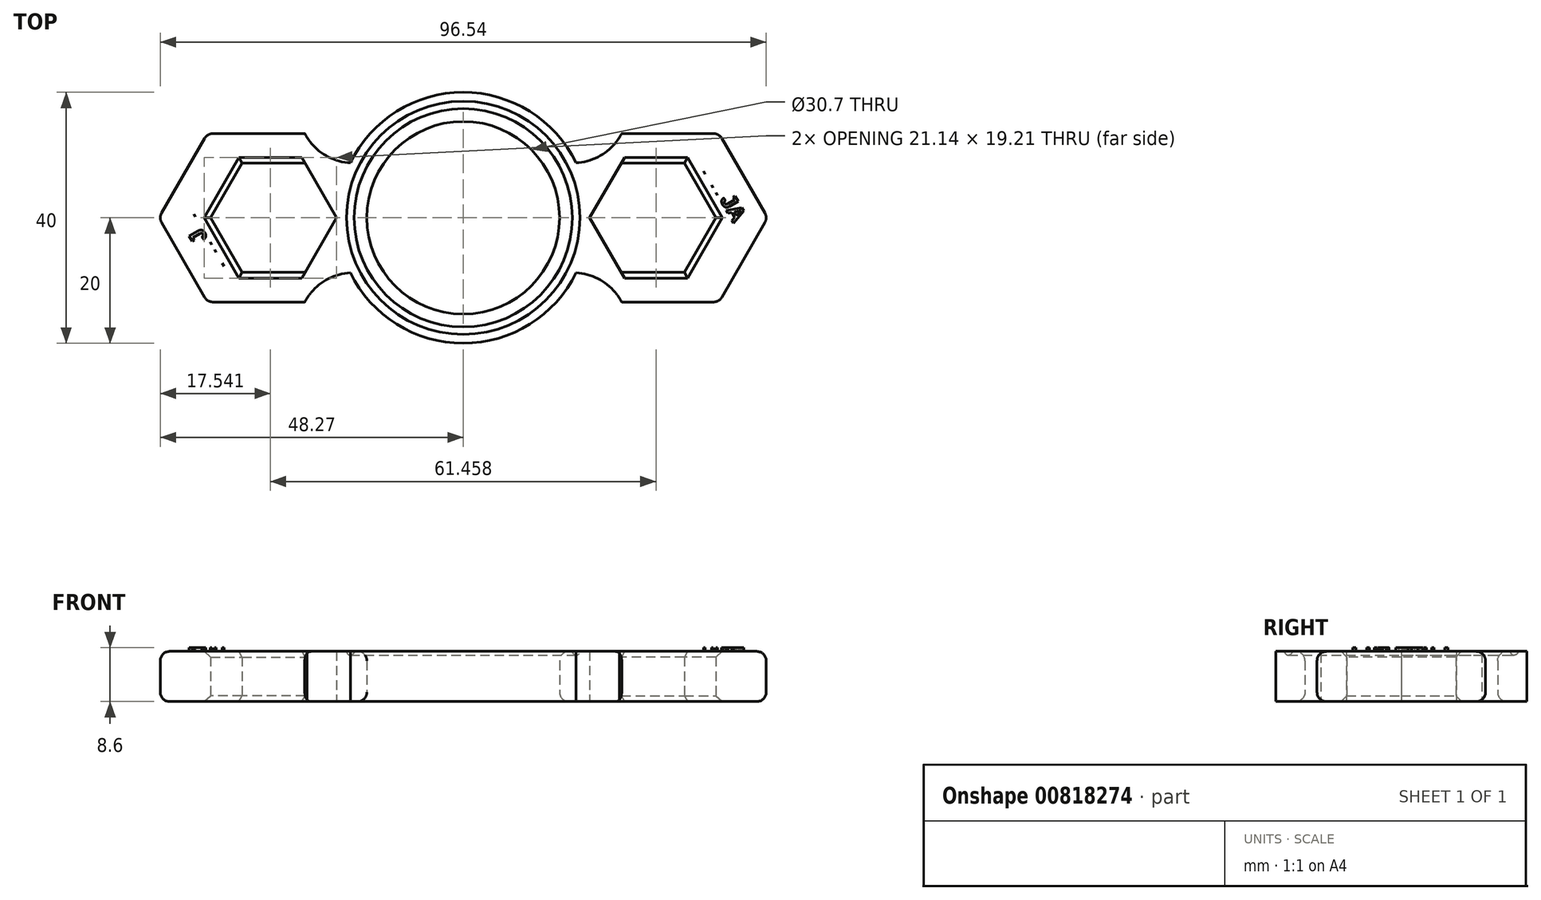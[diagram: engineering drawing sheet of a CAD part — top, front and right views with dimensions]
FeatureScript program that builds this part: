
annotation { "Feature Type Name" : "Feature", "Feature Type Description" : "" }
export const myFeature = defineFeature(function(context is Context, id is Id, definition is map)
    precondition{}
    {
        {
            var Q0;
            Q0=qCreatedBy(makeId("Top.planeOp"),FACE);
            var sketch = newSketch(context, id + "F0", { "sketchPlane" : qUnion([Q0])});
            skCircle(sketch, "E0", {"center": v(0, 0) * mm, "radius": 15.35 * mm});
            skArc(sketch, "E1", {"start": v(14.93, 9.13) * mm, "mid": v(0, 17.5) * mm, "end": v(-14.93, 9.13) * mm});
            skPoint(sketch, "E2.centerSnap0", {"position": v(-30.2, 9.1) * mm});
            skLineSegment(sketch, "E3.0", {"start": v(-24.9, -12.83) * mm, "end": v(-25.25, -13.42) * mm});
            skLineSegment(sketch, "E3.1", {"start": v(-25.25, -13.42) * mm, "end": v(-40.75, -13.42) * mm});
            skLineSegment(sketch, "E3.2", {"start": v(-40.75, -13.42) * mm, "end": v(-48.5, 0) * mm});
            skLineSegment(sketch, "E3.3", {"start": v(-48.5, 0) * mm, "end": v(-40.75, 13.42) * mm});
            skLineSegment(sketch, "E3.4", {"start": v(-40.75, 13.42) * mm, "end": v(-25.25, 13.42) * mm});
            skLineSegment(sketch, "E3.5", {"start": v(-25.25, 13.42) * mm, "end": v(-24.9, 12.83) * mm});
            skLineSegment(sketch, "E4.0", {"start": v(24.9, 12.83) * mm, "end": v(25.25, 13.42) * mm});
            skLineSegment(sketch, "E4.1", {"start": v(25.25, 13.42) * mm, "end": v(40.75, 13.42) * mm});
            skLineSegment(sketch, "E4.2", {"start": v(40.75, 13.42) * mm, "end": v(48.5, 0) * mm});
            skLineSegment(sketch, "E4.3", {"start": v(48.5, 0) * mm, "end": v(40.75, -13.42) * mm});
            skLineSegment(sketch, "E4.4", {"start": v(40.75, -13.42) * mm, "end": v(25.25, -13.42) * mm});
            skLineSegment(sketch, "E4.5", {"start": v(25.25, -13.42) * mm, "end": v(24.9, -12.83) * mm});
            skArc(sketch, "E5", {"start": v(14.93, 9.13) * mm, "mid": v(20.86, 9.42) * mm, "end": v(25.25, 13.42) * mm});
            skArc(sketch, "E6.trimOffspring", {"start": v(25.25, -13.42) * mm, "mid": v(20.86, -9.42) * mm, "end": v(14.93, -9.13) * mm});
            skPoint(sketch, "E7.center.orphan", {"position": v(33, 0) * mm});
            skPoint(sketch, "E8.center.orphan", {"position": v(0, -17.5) * mm});
            skPoint(sketch, "E9.start.orphan", {"position": v(17.5, 0) * mm});
            skArc(sketch, "E10", {"start": v(-14.93, -9.13) * mm, "mid": v(-20.86, -9.42) * mm, "end": v(-25.25, -13.42) * mm});
            skArc(sketch, "E11.trimOffspring", {"start": v(-14.93, -9.13) * mm, "mid": v(0, -17.5) * mm, "end": v(14.93, -9.13) * mm});
            skArc(sketch, "E12", {"start": v(-25.25, 13.42) * mm, "mid": v(-20.86, 9.42) * mm, "end": v(-14.93, 9.13) * mm});
            skPoint(sketch, "E2.center.orphan", {"position": v(-30.2, 0) * mm});
            skPoint(sketch, "E13.center.orphan", {"position": v(0, 17.5) * mm});
            skCircle(sketch, "E14.cCircle", {"center": v(-30.2, 0) * mm, "radius": 10.05 * mm, "construction": true});
            skLineSegment(sketch, "E14.0", {"start": v(-20.16, 0) * mm, "end": v(-25.18, -8.7) * mm});
            skLineSegment(sketch, "E14.1", {"start": v(-25.18, -8.7) * mm, "end": v(-35.23, -8.7) * mm});
            skLineSegment(sketch, "E14.2", {"start": v(-35.23, -8.7) * mm, "end": v(-40.26, 0) * mm});
            skLineSegment(sketch, "E14.3", {"start": v(-40.26, 0) * mm, "end": v(-35.23, 8.7) * mm});
            skLineSegment(sketch, "E14.4", {"start": v(-35.23, 8.7) * mm, "end": v(-25.18, 8.7) * mm});
            skLineSegment(sketch, "E14.5", {"start": v(-25.18, 8.7) * mm, "end": v(-20.16, 0) * mm});
            skPoint(sketch, "E15", {"position": v(-27, 0) * mm});
            skCircle(sketch, "E16.cCircle", {"center": v(30.2, 0) * mm, "radius": 10.05 * mm, "construction": true});
            skLineSegment(sketch, "E16.0", {"start": v(20.16, 0) * mm, "end": v(25.18, 8.7) * mm});
            skLineSegment(sketch, "E16.1", {"start": v(25.18, 8.7) * mm, "end": v(35.23, 8.7) * mm});
            skLineSegment(sketch, "E16.2", {"start": v(35.23, 8.7) * mm, "end": v(40.26, 0) * mm});
            skLineSegment(sketch, "E16.3", {"start": v(40.26, 0) * mm, "end": v(35.23, -8.7) * mm});
            skLineSegment(sketch, "E16.4", {"start": v(35.23, -8.7) * mm, "end": v(25.18, -8.7) * mm});
            skLineSegment(sketch, "E16.5", {"start": v(25.18, -8.7) * mm, "end": v(20.16, 0) * mm});
            skCircle(sketch, "E17", {"center": v(0, 0) * mm, "radius": 20 * mm});
            skLineSegment(sketch, "E18", {"start": v(-24.9, 12.83) * mm, "end": v(-15.35, 12.83) * mm});
            skSolve(sketch);
        }
        {
            var Q0;
            {var subQ0=sQuery(id+"F0.wireOp",EDGE,"E3.0");Q0=makeQuery(id+"F0.imprint","IMPRINT",FACE,{"disambiguationData":[TD([[makeQuery(id+"F0.imprint","IMPRINT",EDGE,{"derivedFrom":subQ0}),-1.0]])]});}
            var Q1;
            {var subQ0=sQuery(id+"F0.wireOp",EDGE,"E3.5");Q1=makeQuery(id+"F0.imprint","IMPRINT",FACE,{"disambiguationData":[TD([[makeQuery(id+"F0.imprint","IMPRINT",EDGE,{"derivedFrom":subQ0}),-1.0]])]});}
            var Q2;
            {var subQ0=sQuery(id+"F0.wireOp",EDGE,"E4.0");Q2=makeQuery(id+"F0.imprint","IMPRINT",FACE,{"disambiguationData":[TD([[makeQuery(id+"F0.imprint","IMPRINT",EDGE,{"derivedFrom":subQ0}),-1.0]])]});}
            var Q3;
            {var subQ0=sQuery(id+"F0.wireOp",EDGE,"E4.5");Q3=makeQuery(id+"F0.imprint","IMPRINT",FACE,{"disambiguationData":[TD([[makeQuery(id+"F0.imprint","IMPRINT",EDGE,{"derivedFrom":subQ0}),-1.0]])]});}
            var Q4;
            {var subQ0=sQuery(id+"F0.wireOp",EDGE,"E11.trimOffspring");Q4=makeQuery(id+"F0.imprint","IMPRINT",FACE,{"disambiguationData":[TD([[makeQuery(id+"F0.imprint","IMPRINT",EDGE,{"derivedFrom":subQ0}),-1.0]])]});}
            var Q5;
            {var subQ4=sQuery(id+"F0.wireOp",EDGE,"E1");Q5=makeQuery(id+"F0.imprint","IMPRINT",FACE,{"disambiguationData":[TD([[makeQuery(id+"F0.imprint","IMPRINT",EDGE,{"derivedFrom":subQ4}),-1.0]])]});}
            var Q6;
            {var subQ9=sQuery(id+"F0.wireOp",EDGE,"E4.1");Q6=makeQuery(id+"F0.imprint","IMPRINT",FACE,{"disambiguationData":[TD([[makeQuery(id+"F0.imprint","IMPRINT",EDGE,{"derivedFrom":subQ9}),-1.0]])]});}
            var Q7;
            Q7=makeQuery(id+"F0.imprint","IMPRINT",FACE,{"disambiguationData":[TD([[makeQuery(id+"F0.imprint","IMPRINT",EDGE,{"derivedFrom":sQuery(id+"F0.wireOp",EDGE,"E0")}),-1.0]])]});
            var Q8;
            {var subQ7=sQuery(id+"F0.wireOp",EDGE,"E3.1");Q8=makeQuery(id+"F0.imprint","IMPRINT",FACE,{"disambiguationData":[TD([[makeQuery(id+"F0.imprint","IMPRINT",EDGE,{"derivedFrom":subQ7}),-1.0]])]});}
            extrude(context, id + "F1", {"entities" : qUnion([Q0, Q1, Q2, Q3, Q4, Q5, Q6, Q7, Q8]), "endBound" : BoundingType.SYMMETRIC, "depth" : 8 * mm, "offsetDistance" : 25 * mm});
        }
        {
            var Q0;
            Q0=makeQuery(id+"F1.opExtrude","CAP_EDGE",EDGE,{"disambiguationData":[OSD([sQuery(id+"F0.wireOp",EDGE,"E4.2")])],"isStart":true});
            var Q1;
            Q1=makeQuery(id+"F1.opExtrude","SWEPT_EDGE",EDGE,{"disambiguationData":[OSD([sQuery(id+"F0.wireOp",EDGE,"E4.1"),sQuery(id+"F0.wireOp",EDGE,"E4.2")])]});
            var Q2;
            Q2=makeQuery(id+"F1.opExtrude","CAP_EDGE",EDGE,{"disambiguationData":[OSD([sQuery(id+"F0.wireOp",EDGE,"E4.2")])],"isStart":false});
            var Q3;
            Q3=makeQuery(id+"F1.opExtrude","SWEPT_EDGE",EDGE,{"disambiguationData":[OSD([sQuery(id+"F0.wireOp",EDGE,"E4.2"),sQuery(id+"F0.wireOp",EDGE,"E4.3")])]});
            var Q4;
            Q4=makeQuery(id+"F1.opExtrude","CAP_EDGE",EDGE,{"disambiguationData":[OSD([sQuery(id+"F0.wireOp",EDGE,"E4.1")])],"isStart":true});
            var Q5;
            Q5=makeQuery(id+"F1.opExtrude","CAP_EDGE",EDGE,{"disambiguationData":[OSD([sQuery(id+"F0.wireOp",EDGE,"E4.1")])],"isStart":false});
            var Q6;
            Q6=makeQuery(id+"F1.opExtrude","CAP_EDGE",EDGE,{"disambiguationData":[OSD([sQuery(id+"F0.wireOp",EDGE,"E4.4")])],"isStart":false});
            var Q7;
            Q7=makeQuery(id+"F1.opExtrude","CAP_EDGE",EDGE,{"disambiguationData":[OSD([sQuery(id+"F0.wireOp",EDGE,"E4.3")])],"isStart":false});
            var Q8;
            Q8=makeQuery(id+"F1.opExtrude","SWEPT_EDGE",EDGE,{"disambiguationData":[OSD([sQuery(id+"F0.wireOp",EDGE,"E4.3"),sQuery(id+"F0.wireOp",EDGE,"E4.4")])]});
            var Q9;
            Q9=makeQuery(id+"F1.opExtrude","CAP_EDGE",EDGE,{"disambiguationData":[OSD([sQuery(id+"F0.wireOp",EDGE,"E4.3")])],"isStart":true});
            var Q10;
            Q10=makeQuery(id+"F1.opExtrude","CAP_EDGE",EDGE,{"disambiguationData":[OSD([sQuery(id+"F0.wireOp",EDGE,"E4.4")])],"isStart":true});
            var Q11;
            Q11=makeQuery(id+"F1.opExtrude","CAP_EDGE",EDGE,{"disambiguationData":[OSD([sQuery(id+"F0.wireOp",EDGE,"E3.1")])],"isStart":true});
            var Q12;
            Q12=makeQuery(id+"F1.opExtrude","CAP_EDGE",EDGE,{"disambiguationData":[OSD([sQuery(id+"F0.wireOp",EDGE,"E3.2")])],"isStart":true});
            var Q13;
            Q13=makeQuery(id+"F1.opExtrude","CAP_EDGE",EDGE,{"disambiguationData":[OSD([sQuery(id+"F0.wireOp",EDGE,"E3.3")])],"isStart":true});
            var Q14;
            Q14=makeQuery(id+"F1.opExtrude","CAP_EDGE",EDGE,{"disambiguationData":[OSD([sQuery(id+"F0.wireOp",EDGE,"E3.4")])],"isStart":true});
            var Q15;
            Q15=makeQuery(id+"F1.opExtrude","CAP_EDGE",EDGE,{"disambiguationData":[OSD([sQuery(id+"F0.wireOp",EDGE,"E3.3")])],"isStart":false});
            var Q16;
            Q16=makeQuery(id+"F1.opExtrude","SWEPT_EDGE",EDGE,{"disambiguationData":[OSD([sQuery(id+"F0.wireOp",EDGE,"E3.2"),sQuery(id+"F0.wireOp",EDGE,"E3.3")])]});
            var Q17;
            Q17=makeQuery(id+"F1.opExtrude","CAP_EDGE",EDGE,{"disambiguationData":[OSD([sQuery(id+"F0.wireOp",EDGE,"E3.2")])],"isStart":false});
            var Q18;
            Q18=makeQuery(id+"F1.opExtrude","CAP_EDGE",EDGE,{"disambiguationData":[OSD([sQuery(id+"F0.wireOp",EDGE,"E3.1")])],"isStart":false});
            var Q19;
            Q19=makeQuery(id+"F1.opExtrude","SWEPT_EDGE",EDGE,{"disambiguationData":[OSD([sQuery(id+"F0.wireOp",EDGE,"E3.1"),sQuery(id+"F0.wireOp",EDGE,"E3.2")])]});
            var Q20;
            Q20=makeQuery(id+"F1.opExtrude","SWEPT_EDGE",EDGE,{"disambiguationData":[OSD([sQuery(id+"F0.wireOp",EDGE,"E3.3"),sQuery(id+"F0.wireOp",EDGE,"E3.4")])]});
            var Q21;
            Q21=makeQuery(id+"F1.opExtrude","CAP_EDGE",EDGE,{"disambiguationData":[OSD([sQuery(id+"F0.wireOp",EDGE,"E3.4")])],"isStart":false});
            var Q22;
            Q22=makeQuery(id+"F1.opExtrude","CAP_EDGE",EDGE,{"disambiguationData":[OSD([sQuery(id+"F0.wireOp",EDGE,"6d71efc6-a7b5-46e8-b336-96c0588495bb.4")])],"isStart":false});
            var Q23;
            Q23=makeQuery(id+"F1.opExtrude","CAP_EDGE",EDGE,{"disambiguationData":[OSD([sQuery(id+"F0.wireOp",EDGE,"6d71efc6-a7b5-46e8-b336-96c0588495bb.5")])],"isStart":false});
            var Q24;
            Q24=makeQuery(id+"F1.opExtrude","CAP_EDGE",EDGE,{"disambiguationData":[OSD([sQuery(id+"F0.wireOp",EDGE,"6d71efc6-a7b5-46e8-b336-96c0588495bb.0")])],"isStart":false});
            var Q25;
            Q25=makeQuery(id+"F1.opExtrude","CAP_EDGE",EDGE,{"disambiguationData":[OSD([sQuery(id+"F0.wireOp",EDGE,"6d71efc6-a7b5-46e8-b336-96c0588495bb.1")])],"isStart":false});
            var Q26;
            Q26=makeQuery(id+"F1.opExtrude","CAP_EDGE",EDGE,{"disambiguationData":[OSD([sQuery(id+"F0.wireOp",EDGE,"6d71efc6-a7b5-46e8-b336-96c0588495bb.2")])],"isStart":false});
            var Q27;
            Q27=makeQuery(id+"F1.opExtrude","CAP_EDGE",EDGE,{"disambiguationData":[OSD([sQuery(id+"F0.wireOp",EDGE,"6d71efc6-a7b5-46e8-b336-96c0588495bb.3")])],"isStart":false});
            var Q28;
            Q28=makeQuery(id+"F1.opExtrude","CAP_EDGE",EDGE,{"disambiguationData":[OSD([sQuery(id+"F0.wireOp",EDGE,"6d71efc6-a7b5-46e8-b336-96c0588495bb.0")])],"isStart":true});
            var Q29;
            Q29=makeQuery(id+"F1.opExtrude","CAP_EDGE",EDGE,{"disambiguationData":[OSD([sQuery(id+"F0.wireOp",EDGE,"6d71efc6-a7b5-46e8-b336-96c0588495bb.5")])],"isStart":true});
            var Q30;
            Q30=makeQuery(id+"F1.opExtrude","CAP_EDGE",EDGE,{"disambiguationData":[OSD([sQuery(id+"F0.wireOp",EDGE,"6d71efc6-a7b5-46e8-b336-96c0588495bb.4")])],"isStart":true});
            var Q31;
            Q31=makeQuery(id+"F1.opExtrude","CAP_EDGE",EDGE,{"disambiguationData":[OSD([sQuery(id+"F0.wireOp",EDGE,"6d71efc6-a7b5-46e8-b336-96c0588495bb.3")])],"isStart":true});
            var Q32;
            Q32=makeQuery(id+"F1.opExtrude","CAP_EDGE",EDGE,{"disambiguationData":[OSD([sQuery(id+"F0.wireOp",EDGE,"6d71efc6-a7b5-46e8-b336-96c0588495bb.2")])],"isStart":true});
            var Q33;
            Q33=makeQuery(id+"F1.opExtrude","CAP_EDGE",EDGE,{"disambiguationData":[OSD([sQuery(id+"F0.wireOp",EDGE,"6d71efc6-a7b5-46e8-b336-96c0588495bb.1")])],"isStart":true});
            var Q34;
            Q34=makeQuery(id+"F1.opExtrude","CAP_EDGE",EDGE,{"disambiguationData":[OSD([sQuery(id+"F0.wireOp",EDGE,"79f7cf52-5bca-44dd-9481-65be4d3bd6c9.5")])],"isStart":true});
            var Q35;
            Q35=makeQuery(id+"F1.opExtrude","CAP_EDGE",EDGE,{"disambiguationData":[OSD([sQuery(id+"F0.wireOp",EDGE,"79f7cf52-5bca-44dd-9481-65be4d3bd6c9.4")])],"isStart":true});
            var Q36;
            Q36=makeQuery(id+"F1.opExtrude","CAP_EDGE",EDGE,{"disambiguationData":[OSD([sQuery(id+"F0.wireOp",EDGE,"79f7cf52-5bca-44dd-9481-65be4d3bd6c9.3")])],"isStart":true});
            var Q37;
            Q37=makeQuery(id+"F1.opExtrude","CAP_EDGE",EDGE,{"disambiguationData":[OSD([sQuery(id+"F0.wireOp",EDGE,"79f7cf52-5bca-44dd-9481-65be4d3bd6c9.2")])],"isStart":true});
            var Q38;
            Q38=makeQuery(id+"F1.opExtrude","CAP_EDGE",EDGE,{"disambiguationData":[OSD([sQuery(id+"F0.wireOp",EDGE,"79f7cf52-5bca-44dd-9481-65be4d3bd6c9.1")])],"isStart":true});
            var Q39;
            Q39=makeQuery(id+"F1.opExtrude","CAP_EDGE",EDGE,{"disambiguationData":[OSD([sQuery(id+"F0.wireOp",EDGE,"79f7cf52-5bca-44dd-9481-65be4d3bd6c9.0")])],"isStart":true});
            var Q40;
            Q40=makeQuery(id+"F1.opExtrude","CAP_EDGE",EDGE,{"disambiguationData":[OSD([sQuery(id+"F0.wireOp",EDGE,"79f7cf52-5bca-44dd-9481-65be4d3bd6c9.4")])],"isStart":false});
            var Q41;
            Q41=makeQuery(id+"F1.opExtrude","CAP_EDGE",EDGE,{"disambiguationData":[OSD([sQuery(id+"F0.wireOp",EDGE,"79f7cf52-5bca-44dd-9481-65be4d3bd6c9.3")])],"isStart":false});
            var Q42;
            Q42=makeQuery(id+"F1.opExtrude","CAP_EDGE",EDGE,{"disambiguationData":[OSD([sQuery(id+"F0.wireOp",EDGE,"79f7cf52-5bca-44dd-9481-65be4d3bd6c9.2")])],"isStart":false});
            var Q43;
            Q43=makeQuery(id+"F1.opExtrude","CAP_EDGE",EDGE,{"disambiguationData":[OSD([sQuery(id+"F0.wireOp",EDGE,"79f7cf52-5bca-44dd-9481-65be4d3bd6c9.5")])],"isStart":false});
            var Q44;
            Q44=makeQuery(id+"F1.opExtrude","CAP_EDGE",EDGE,{"disambiguationData":[OSD([sQuery(id+"F0.wireOp",EDGE,"79f7cf52-5bca-44dd-9481-65be4d3bd6c9.0")])],"isStart":false});
            var Q45;
            Q45=makeQuery(id+"F1.opExtrude","CAP_EDGE",EDGE,{"disambiguationData":[OSD([sQuery(id+"F0.wireOp",EDGE,"79f7cf52-5bca-44dd-9481-65be4d3bd6c9.1")])],"isStart":false});
            var Q46;
            Q46=makeQuery(id+"F1.opExtrude","CAP_EDGE",EDGE,{"disambiguationData":[OSD([sQuery(id+"F0.wireOp",EDGE,"E0")])],"isStart":false});
            var Q47;
            Q47=makeQuery(id+"F1.opExtrude","CAP_EDGE",EDGE,{"disambiguationData":[OSD([sQuery(id+"F0.wireOp",EDGE,"E0")])],"isStart":true});
            fillet(context, id + "F2", {"entities" : qUnion([Q0, Q1, Q2, Q3, Q4, Q5, Q6, Q7, Q8, Q9, Q10, Q11, Q12, Q13, Q14, Q15, Q16, Q17, Q18, Q19, Q20, Q21, Q22, Q23, Q24, Q25, Q26, Q27, Q28, Q29, Q30, Q31, Q32, Q33, Q34, Q35, Q36, Q37, Q38, Q39, Q40, Q41, Q42, Q43, Q44, Q45, Q46, Q47]), "radius" : 1.5 * mm, "tangentPropagation" : true, "allowEdgeOverflow" : false});
        }
        {
            var Q0;
            Q0=makeQuery(id+"F1.opExtrude","CAP_EDGE",EDGE,{"disambiguationData":[OSD([sQuery(id+"F0.wireOp",EDGE,"E16.1")])],"isStart":false});
            var Q1;
            Q1=makeQuery(id+"F1.opExtrude","CAP_EDGE",EDGE,{"disambiguationData":[OSD([sQuery(id+"F0.wireOp",EDGE,"E16.1")])],"isStart":true});
            var Q2;
            Q2=makeQuery(id+"F1.opExtrude","CAP_EDGE",EDGE,{"disambiguationData":[OSD([sQuery(id+"F0.wireOp",EDGE,"E16.2")])],"isStart":true});
            var Q3;
            Q3=makeQuery(id+"F1.opExtrude","CAP_EDGE",EDGE,{"disambiguationData":[OSD([sQuery(id+"F0.wireOp",EDGE,"E16.2")])],"isStart":false});
            var Q4;
            Q4=makeQuery(id+"F1.opExtrude","CAP_EDGE",EDGE,{"disambiguationData":[OSD([sQuery(id+"F0.wireOp",EDGE,"E16.3")])],"isStart":false});
            var Q5;
            Q5=makeQuery(id+"F1.opExtrude","CAP_EDGE",EDGE,{"disambiguationData":[OSD([sQuery(id+"F0.wireOp",EDGE,"E16.3")])],"isStart":true});
            var Q6;
            Q6=makeQuery(id+"F1.opExtrude","CAP_EDGE",EDGE,{"disambiguationData":[OSD([sQuery(id+"F0.wireOp",EDGE,"E16.4")])],"isStart":false});
            var Q7;
            Q7=makeQuery(id+"F1.opExtrude","CAP_EDGE",EDGE,{"disambiguationData":[OSD([sQuery(id+"F0.wireOp",EDGE,"E14.4")])],"isStart":false});
            var Q8;
            Q8=makeQuery(id+"F1.opExtrude","CAP_EDGE",EDGE,{"disambiguationData":[OSD([sQuery(id+"F0.wireOp",EDGE,"E14.3")])],"isStart":false});
            var Q9;
            Q9=makeQuery(id+"F1.opExtrude","CAP_EDGE",EDGE,{"disambiguationData":[OSD([sQuery(id+"F0.wireOp",EDGE,"E14.2")])],"isStart":false});
            var Q10;
            Q10=makeQuery(id+"F1.opExtrude","CAP_EDGE",EDGE,{"disambiguationData":[OSD([sQuery(id+"F0.wireOp",EDGE,"E14.1")])],"isStart":false});
            var Q11;
            Q11=makeQuery(id+"F1.opExtrude","CAP_EDGE",EDGE,{"disambiguationData":[OSD([sQuery(id+"F0.wireOp",EDGE,"E16.4")])],"isStart":true});
            var Q12;
            Q12=makeQuery(id+"F1.opExtrude","CAP_EDGE",EDGE,{"disambiguationData":[OSD([sQuery(id+"F0.wireOp",EDGE,"E14.3")])],"isStart":true});
            var Q13;
            Q13=makeQuery(id+"F1.opExtrude","CAP_EDGE",EDGE,{"disambiguationData":[OSD([sQuery(id+"F0.wireOp",EDGE,"E14.2")])],"isStart":true});
            var Q14;
            Q14=makeQuery(id+"F1.opExtrude","CAP_EDGE",EDGE,{"disambiguationData":[OSD([sQuery(id+"F0.wireOp",EDGE,"E14.1")])],"isStart":true});
            var Q15;
            Q15=makeQuery(id+"F1.opExtrude","CAP_EDGE",EDGE,{"disambiguationData":[OSD([sQuery(id+"F0.wireOp",EDGE,"E14.4")])],"isStart":true});
            chamfer(context, id + "F3", {"entities" : qUnion([Q0, Q1, Q2, Q3, Q4, Q5, Q6, Q7, Q8, Q9, Q10, Q11, Q12, Q13, Q14, Q15]), "width" : 0.9 * mm, "tangentPropagation" : true});
        }
        {
            var Q0;
            Q0=makeQuery(id+"F1.opExtrude","CAP_FACE",FACE,{"disambiguationData":[OSD([sQuery(id+"F0.wireOp",EDGE,"E0"),sQuery(id+"F0.wireOp",EDGE,"E3.0"),sQuery(id+"F0.wireOp",EDGE,"E3.1"),sQuery(id+"F0.wireOp",EDGE,"E3.2"),sQuery(id+"F0.wireOp",EDGE,"E3.3"),sQuery(id+"F0.wireOp",EDGE,"E3.4"),sQuery(id+"F0.wireOp",EDGE,"E3.5"),sQuery(id+"F0.wireOp",EDGE,"E4.0"),sQuery(id+"F0.wireOp",EDGE,"E4.1"),sQuery(id+"F0.wireOp",EDGE,"E4.2"),sQuery(id+"F0.wireOp",EDGE,"E4.3"),sQuery(id+"F0.wireOp",EDGE,"E4.4"),sQuery(id+"F0.wireOp",EDGE,"E4.5"),sQuery(id+"F0.wireOp",EDGE,"E5"),sQuery(id+"F0.wireOp",EDGE,"E6.trimOffspring"),sQuery(id+"F0.wireOp",EDGE,"E10"),sQuery(id+"F0.wireOp",EDGE,"E12"),sQuery(id+"F0.wireOp",EDGE,"E14.0"),sQuery(id+"F0.wireOp",EDGE,"E14.1"),sQuery(id+"F0.wireOp",EDGE,"E14.2"),sQuery(id+"F0.wireOp",EDGE,"E14.3"),sQuery(id+"F0.wireOp",EDGE,"E14.4"),sQuery(id+"F0.wireOp",EDGE,"E14.5"),sQuery(id+"F0.wireOp",EDGE,"E16.0"),sQuery(id+"F0.wireOp",EDGE,"E16.1"),sQuery(id+"F0.wireOp",EDGE,"E16.2"),sQuery(id+"F0.wireOp",EDGE,"E16.3"),sQuery(id+"F0.wireOp",EDGE,"E16.4"),sQuery(id+"F0.wireOp",EDGE,"E16.5"),sQuery(id+"F0.wireOp",EDGE,"E17")])],"isStart":false});
            var sketch = newSketch(context, id + "F4", { "sketchPlane" : qUnion([Q0])});
            skLineSegment(sketch, "E19", {"start": v(36.26, 10.93) * mm, "end": v(42.57, 0) * mm});
            skLineSegment(sketch, "E20", {"start": v(-43.33, 1.33) * mm, "end": v(-37.17, -9.35) * mm});
            skText(sketch, "E21", { "text": "KATJA", "fontName": "Arimo-Bold.ttf"});
            skText(sketch, "E22", { "text": "KATJA", "fontName": "Arimo-Bold.ttf"});
            skCircle(sketch, "E23", {"center": v(0, 0) * mm, "radius": 18 * mm});
            const initialGuessF4  = {"E21": [-0.03717, -0.00935, -0.5, 0.86603, 0.0025], "E22": [0.03733, 0.00907, 0.5, -0.86603, 0.0025]};
            skSetInitialGuess(sketch, initialGuessF4);
            skSolve(sketch);
        }
        {
            var Q0;
            Q0=makeQuery(id+"F4.imprint","IMPRINT",FACE,{"disambiguationData":[TD([[makeQuery(id+"F4.imprint","IMPRINT",EDGE,{"derivedFrom":sQuery(id+"F4.wireOp",EDGE,"E21.sketch_text.stroke-27")}),-1.0]])]});
            var Q1;
            Q1=makeQuery(id+"F4.imprint","IMPRINT",FACE,{"disambiguationData":[TD([[makeQuery(id+"F4.imprint","IMPRINT",EDGE,{"derivedFrom":sQuery(id+"F4.wireOp",EDGE,"E22.sketch_text.stroke-27")}),-1.0]])]});
            var Q2;
            {var subQ0=sQuery(id+"F4.wireOp",EDGE,"E22.sketch_text.stroke-35");var subQ1=sQuery(id+"F4.wireOp",EDGE,"E19");var subQ2=makeQuery(id+"F4.imprint","INTERSECT",VERTEX,{"derivedFrom":[subQ1,subQ0]});Q2=makeQuery(id+"F4.imprint","IMPRINT",FACE,{"disambiguationData":[TD([[makeQuery(id+"F4.imprint","IMPRINT",EDGE,{"disambiguationData":[TD([[subQ2,-1.0]])],"derivedFrom":subQ1}),-1.0]])]});}
            var Q3;
            {var subQ5=sQuery(id+"F4.wireOp",EDGE,"E22.sketch_text.stroke-36");Q3=makeQuery(id+"F4.imprint","IMPRINT",FACE,{"disambiguationData":[TD([[makeQuery(id+"F4.imprint","IMPRINT",EDGE,{"derivedFrom":subQ5}),-1.0]])]});}
            var Q4;
            {var subQ0=sQuery(id+"F4.wireOp",EDGE,"E21.sketch_text.stroke-35");var subQ1=sQuery(id+"F4.wireOp",EDGE,"E20");var subQ2=makeQuery(id+"F4.imprint","INTERSECT",VERTEX,{"derivedFrom":[subQ1,subQ0]});Q4=makeQuery(id+"F4.imprint","IMPRINT",FACE,{"disambiguationData":[TD([[makeQuery(id+"F4.imprint","IMPRINT",EDGE,{"disambiguationData":[TD([[subQ2,1.0]])],"derivedFrom":subQ1}),1.0]])]});}
            var Q5;
            {var subQ5=sQuery(id+"F4.wireOp",EDGE,"E21.sketch_text.stroke-36");Q5=makeQuery(id+"F4.imprint","IMPRINT",FACE,{"disambiguationData":[TD([[makeQuery(id+"F4.imprint","IMPRINT",EDGE,{"derivedFrom":subQ5}),-1.0]])]});}
            var Q6;
            Q6=makeQuery(id+"F4.imprint","IMPRINT",FACE,{"disambiguationData":[TD([[makeQuery(id+"F4.imprint","IMPRINT",EDGE,{"derivedFrom":sQuery(id+"F4.wireOp",EDGE,"E21.sketch_text.stroke-0")}),-1.0]])]});
            var Q7;
            Q7=makeQuery(id+"F4.imprint","IMPRINT",FACE,{"disambiguationData":[TD([[makeQuery(id+"F4.imprint","IMPRINT",EDGE,{"derivedFrom":sQuery(id+"F4.wireOp",EDGE,"E22.sketch_text.stroke-0")}),-1.0]])]});
            var Q8;
            Q8=makeQuery(id+"F4.imprint","IMPRINT",FACE,{"disambiguationData":[TD([[makeQuery(id+"F4.imprint","IMPRINT",EDGE,{"derivedFrom":sQuery(id+"F4.wireOp",EDGE,"E22.sketch_text.stroke-49")}),-1.0]])]});
            var Q9;
            Q9=makeQuery(id+"F4.imprint","IMPRINT",FACE,{"disambiguationData":[TD([[makeQuery(id+"F4.imprint","IMPRINT",EDGE,{"derivedFrom":sQuery(id+"F4.wireOp",EDGE,"E21.sketch_text.stroke-12")}),-1.0]])]});
            var Q10;
            Q10=makeQuery(id+"F4.imprint","IMPRINT",FACE,{"disambiguationData":[TD([[makeQuery(id+"F4.imprint","IMPRINT",EDGE,{"derivedFrom":sQuery(id+"F4.wireOp",EDGE,"E21.sketch_text.stroke-49")}),-1.0]])]});
            var Q11;
            Q11=makeQuery(id+"F4.imprint","IMPRINT",FACE,{"disambiguationData":[TD([[makeQuery(id+"F4.imprint","IMPRINT",EDGE,{"derivedFrom":sQuery(id+"F4.wireOp",EDGE,"E22.sketch_text.stroke-12")}),-1.0]])]});
            extrude(context, id + "F5", {"entities" : qUnion([Q0, Q1, Q2, Q3, Q4, Q5, Q6, Q7, Q8, Q9, Q10, Q11]), "operationType" : NewBodyOperationType.ADD, "depth" : 0.6 * mm, "offsetDistance" : 25 * mm});
        }
        {
            var Q0;
            Q0=qCreatedBy(makeId("Right.planeOp"),FACE);
            var sketch = newSketch(context, id + "F6", { "sketchPlane" : qUnion([Q0])});
            skCircle(sketch, "E24", {"center": v(17.99, 4) * mm, "radius": 0.6 * mm});
            skLineSegment(sketch, "E25", {"start": v(0, 7.13) * mm, "end": v(0, -7.32) * mm, "construction": true});
            skSolve(sketch);
        }
        {
            var Q0;
            Q0=makeQuery(id+"F6.imprint","IMPRINT",FACE,{"disambiguationData":[TD([[makeQuery(id+"F6.imprint","IMPRINT",EDGE,{"derivedFrom":sQuery(id+"F6.wireOp",EDGE,"E24")}),1.0]])]});
            var Q1;
            Q1=sQuery(id+"F6.wireOp",EDGE,"E25");
            revolve(context, id + "F7", {"operationType" : NewBodyOperationType.REMOVE, "surfaceOperationType" : NewSurfaceOperationType.NEW, "entities" : qUnion([Q0]), "axis" : qUnion([Q1]), "revolveType" : RevolveType.FULL});
        }
    });
